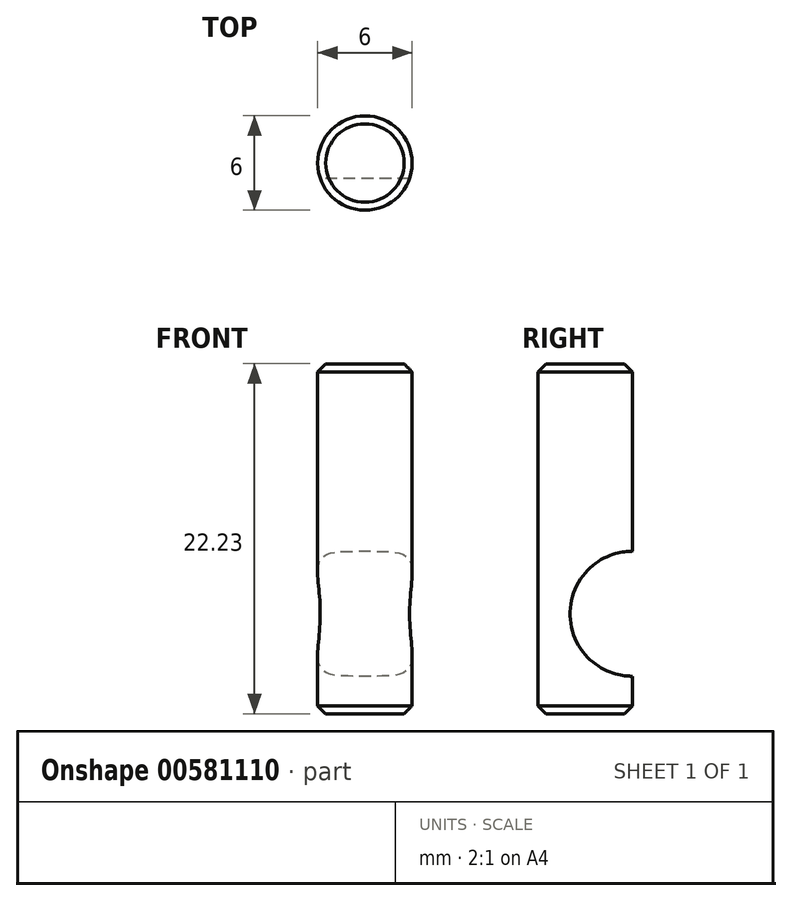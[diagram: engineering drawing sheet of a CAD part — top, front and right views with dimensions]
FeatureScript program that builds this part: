
annotation { "Feature Type Name" : "Feature", "Feature Type Description" : "" }
export const myFeature = defineFeature(function(context is Context, id is Id, definition is map)
    precondition{}
    {
        {
            var Q0;
            Q0=qCreatedBy(makeId("Top.planeOp"),FACE);
            var sketch = newSketch(context, id + "F0", { "sketchPlane" : qUnion([Q0])});
            skCircle(sketch, "E0", {"center": v(0, 0) * mm, "radius": 3 * mm});
            skSolve(sketch);
        }
        {
            var Q0;
            Q0=makeQuery(id+"F0.imprint","IMPRINT",FACE,{"disambiguationData":[TD([[makeQuery(id+"F0.imprint","IMPRINT",EDGE,{"derivedFrom":sQuery(id+"F0.wireOp",EDGE,"E0")}),1.0]])]});
            extrude(context, id + "F1", {"entities" : qUnion([Q0]), "depth" : 22.22 * mm, "offsetDistance" : 25.4 * mm});
        }
        {
            var Q0;
            Q0=qCreatedBy(makeId("Right.planeOp"),FACE);
            var sketch = newSketch(context, id + "F2", { "sketchPlane" : qUnion([Q0])});
            skCircle(sketch, "E1", {"center": v(3, 6.35) * mm, "radius": 3.97 * mm});
            skSolve(sketch);
        }
        {
            var Q0;
            Q0=makeQuery(id+"F2.imprint","IMPRINT",FACE,{"disambiguationData":[TD([[makeQuery(id+"F2.imprint","IMPRINT",EDGE,{"derivedFrom":sQuery(id+"F2.wireOp",EDGE,"E1")}),1.0]])]});
            extrude(context, id + "F3", {"entities" : qUnion([Q0]), "endBound" : BoundingType.SYMMETRIC, "depth" : 25.4 * mm, "offsetDistance" : 25.4 * mm});
        }
        {
            var Q0;
            Q0=makeQuery(id+"F3.opExtrude","SWEPT_BODY",BODY,{"disambiguationData":[OSD([sQuery(id+"F2.wireOp",EDGE,"E1")])]});
            var Q1;
            Q1=makeQuery(id+"F1.opExtrude","SWEPT_BODY",BODY,{"disambiguationData":[OSD([sQuery(id+"F0.wireOp",EDGE,"E0")])]});
            booleanBodies(context, id + "F4", {"operationType" : BooleanOperationType.SUBTRACTION, "tools" : qUnion([Q0]), "targets" : qUnion([Q1])});
        }
        {
            var Q0;
            Q0=makeQuery(id+"F1.opExtrude","CAP_EDGE",EDGE,{"disambiguationData":[OSD([sQuery(id+"F0.wireOp",EDGE,"E0")])],"isStart":false});
            var Q1;
            Q1=makeQuery(id+"F1.opExtrude","CAP_EDGE",EDGE,{"disambiguationData":[OSD([sQuery(id+"F0.wireOp",EDGE,"E0")])],"isStart":true});
            chamfer(context, id + "F5", {"entities" : qUnion([Q0, Q1]), "width" : 0.5 * mm, "tangentPropagation" : true});
        }
    });
